# Revit family: JAD_Retro_H2363_BIM_DE
name_source: partatom
category: Plumbing Fixtures
revit_build: Autodesk Revit 2015 (Build: 20140606_1530(x64)
units: mm (PartAtom-declared; Revit-internal decimal feet)

## types (1)
- H2363A9 - RETRO SL BAS.MIX. W/ EXC. EM
    Accessories = www.idealspec.co.uk
    AreaUnits = millimeters
    Assembly Code = C1030200
    AssetType = Fixed
    BIMObjectName = JAD_Jado_WashbasinTaps_Retro_H2363
    BarCode = 4015234384990
    Brand = Ideal Standard
    Color = Chromium Plated
    ConnectionType = Plumbing
    Cost = 0 $
    Description = RETRO SL BAS.MIX. W/ EXC. EM
    DurationUnit = year
    Features = RETRO SL BAS.MIX. W/ EXC. EM
    Finish = Chromium Plated
    Help = www.idealstandard.de
    IfcExportAs = IfcValveType
    IfcExportType = BASIN MIXER
    InstallationInstructions = www.idealstandard.de
    LinearUnits = millimeters
    MainColor = Chromium Plated
    MaintenanceInformation = www.idealstandard.de
    Manufacturer = www.idealstandard.de
    ManufacturerURL = www.idealstandard.de
    Model = H2363A9
    ModelNumber = H2363A9
    ModelReference = RETRO SL BAS.MIX. W/ EXC. EM
    Name = WashbasinTaps_Retro_H2363_JAD
    NettWeight = 2,66 KG
    NominalDepth = 430 mm
    NominalHeight = 114 mm
    NominalLength = 430 mm
    NominalWidth = 235 mm
    ProductInformation = www.idealstandard.de
    Shape = Sculptured
    Size = 114 x 430 x 235 mm
    Space = Internal
    SpareParts = www.idealstandard.de
    TestPressure = 10 bar
    URL = www.idealstandard.de
    Uniclass2015Code = Pr_40_20_87_98
    Uniclass2015Title = Washbasin taps
    Uniclass2015Version = Products v1.1

## geometry (parser evidence)
native form markers: Blend x4
no freeform markers — native parametric forms only
